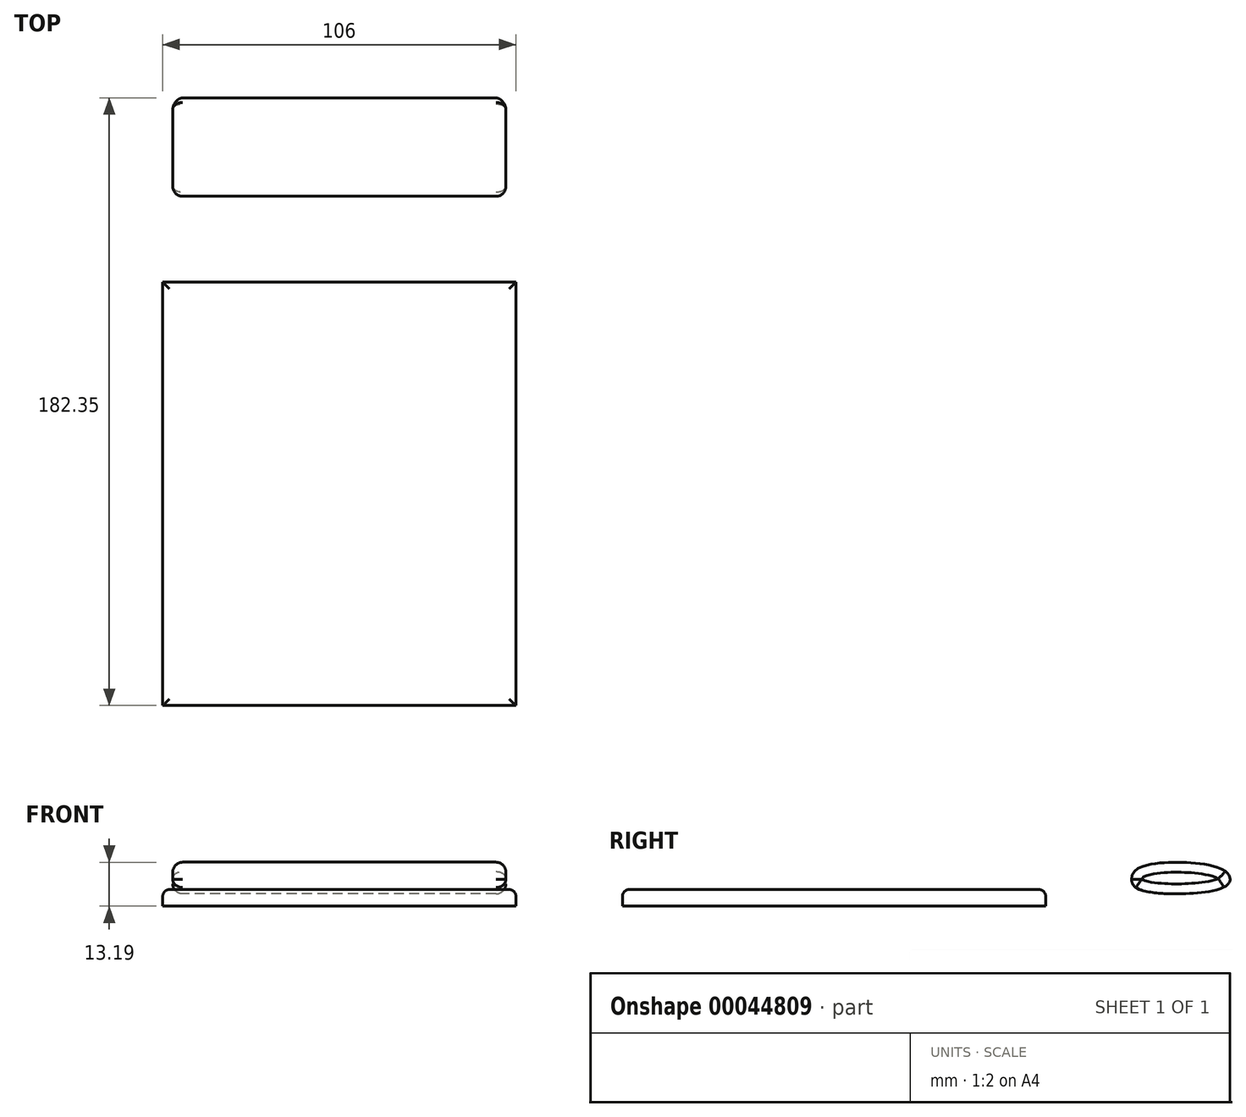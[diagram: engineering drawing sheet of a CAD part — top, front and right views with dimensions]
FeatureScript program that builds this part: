
annotation { "Feature Type Name" : "Feature", "Feature Type Description" : "" }
export const myFeature = defineFeature(function(context is Context, id is Id, definition is map)
    precondition{}
    {
        {
            var Q0;
            Q0=qCreatedBy(makeId("Top.planeOp"),FACE);
            var sketch = newSketch(context, id + "F0", { "sketchPlane" : qUnion([Q0])});
            skLineSegment(sketch, "E0.rect.bottom", {"start": v(108, -11.36) * mm, "end": v(2, -11.36) * mm});
            skLineSegment(sketch, "E0.rect.top", {"start": v(108, -138.36) * mm, "end": v(2, -138.36) * mm});
            skLineSegment(sketch, "E0.rect.left", {"start": v(108, -11.36) * mm, "end": v(108, -138.36) * mm});
            skLineSegment(sketch, "E0.rect.right", {"start": v(2, -11.36) * mm, "end": v(2, -138.36) * mm});
            skPoint(sketch, "E0.rect.middle", {"position": v(55, -74.86) * mm});
            skSolve(sketch);
        }
        {
            var Q0;
            Q0=makeQuery(id+"F0.imprint","IMPRINT",FACE,{"disambiguationData":[TD([[makeQuery(id+"F0.imprint","IMPRINT",EDGE,{"derivedFrom":sQuery(id+"F0.wireOp",EDGE,"E0.rect.bottom")}),1.0]])]});
            extrude(context, id + "F1", {"entities" : qUnion([Q0]), "depth" : 5 * mm});
        }
        {
            var Q0;
            Q0=makeQuery(id+"F1.opExtrude","CAP_EDGE",EDGE,{"disambiguationData":[OSD([sQuery(id+"F0.wireOp",EDGE,"E0.rect.left")])],"isStart":false});
            var Q1;
            Q1=makeQuery(id+"F1.opExtrude","CAP_EDGE",EDGE,{"disambiguationData":[OSD([sQuery(id+"F0.wireOp",EDGE,"E0.rect.bottom")])],"isStart":false});
            var Q2;
            Q2=makeQuery(id+"F1.opExtrude","CAP_EDGE",EDGE,{"disambiguationData":[OSD([sQuery(id+"F0.wireOp",EDGE,"E0.rect.right")])],"isStart":false});
            var Q3;
            Q3=makeQuery(id+"F1.opExtrude","CAP_EDGE",EDGE,{"disambiguationData":[OSD([sQuery(id+"F0.wireOp",EDGE,"E0.rect.top")])],"isStart":false});
            fillet(context, id + "F2", {"entities" : qUnion([Q0, Q1, Q2, Q3]), "radius" : 2 * mm, "tangentPropagation" : true, "allowEdgeOverflow" : false});
        }
        {
            var Q0;
            {var subQ0=sQuery(id+"F0.wireOp",EDGE,"E0.rect.top");Q0=makeQuery(id+"F2.opFillet","BLEND_EDGE",EDGE,{"blendedFrom":[makeQuery(id+"F1.opExtrude","CAP_EDGE",EDGE,{"disambiguationData":[OSD([subQ0])],"isStart":false}),makeQuery(id+"F1.opExtrude","CAP_FACE",FACE,{"disambiguationData":[OSD([sQuery(id+"F0.wireOp",EDGE,"E0.rect.bottom"),subQ0,sQuery(id+"F0.wireOp",EDGE,"E0.rect.left"),sQuery(id+"F0.wireOp",EDGE,"E0.rect.right")])],"isStart":false})],"blendedInto":[makeQuery(id+"F1.opExtrude","CAP_FACE",FACE,{"disambiguationData":[OSD([sQuery(id+"F0.wireOp",EDGE,"E0.rect.bottom"),subQ0,sQuery(id+"F0.wireOp",EDGE,"E0.rect.left"),sQuery(id+"F0.wireOp",EDGE,"E0.rect.right")])],"isStart":false})]});}
            cPlane(context, id + "F3", {"entities" : qUnion([Q0]), "cplaneType" : CPlaneType.MID_PLANE, "offset" : 150 * mm, "width" : 150 * mm, "height" : 150 * mm});
        }
        {
            var Q0;
            Q0=qCreatedBy(id+"F3.planeOp",FACE);
            var sketch = newSketch(context, id + "F4", { "sketchPlane" : qUnion([Q0])});
            skFitSpline(sketch, "E1", {"points": [v(16.89, 5) * mm, v(14.42, 8) * mm, v(16.89, 11.6) * mm, v(40.31, 11.6) * mm, v(43.98, 8) * mm, v(40.31, 5) * mm, v(16.89, 5) * mm]});
            skSolve(sketch);
        }
        {
            var Q0;
            Q0=makeQuery(id+"F4.imprint","IMPRINT",FACE,{"disambiguationData":[TD([[makeQuery(id+"F4.imprint","IMPRINT",EDGE,{"derivedFrom":sQuery(id+"F4.wireOp",EDGE,"E1")}),-1.0]])]});
            extrude(context, id + "F5", {"entities" : qUnion([Q0]), "operationType" : NewBodyOperationType.ADD, "depth" : 50 * mm, "hasSecondDirection" : true, "secondDirectionOppositeDirection" : true, "secondDirectionDepth" : 50 * mm});
        }
        {
            var Q0;
            Q0=makeQuery(id+"F5.opExtrude","CAP_EDGE",EDGE,{"disambiguationData":[OSD([sQuery(id+"F4.wireOp",EDGE,"E1")])],"isStart":false});
            var Q1;
            Q1=makeQuery(id+"F5.opExtrude","CAP_EDGE",EDGE,{"disambiguationData":[OSD([sQuery(id+"F4.wireOp",EDGE,"E1")])],"isStart":true});
            fillet(context, id + "F6", {"entities" : qUnion([Q0, Q1]), "radius" : 3 * mm, "tangentPropagation" : true, "allowEdgeOverflow" : false});
        }
    });
